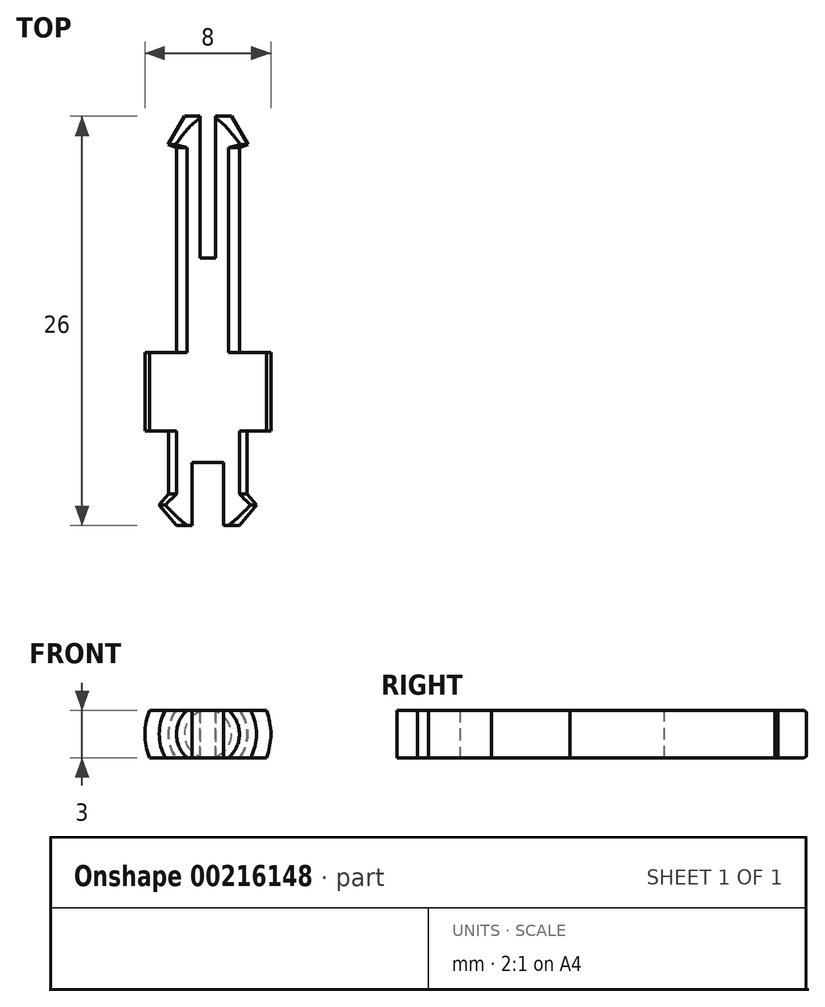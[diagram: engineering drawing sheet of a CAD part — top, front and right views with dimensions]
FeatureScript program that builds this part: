
annotation { "Feature Type Name" : "Feature", "Feature Type Description" : "" }
export const myFeature = defineFeature(function(context is Context, id is Id, definition is map)
    precondition{}
    {
        {
            var Q0;
            Q0=qCreatedBy(makeId("Front.planeOp"),FACE);
            var sketch = newSketch(context, id + "F15", { "sketchPlane" : qUnion([Q0])});
            skCircle(sketch, "E0", {"center": v(0, 0) * mm, "radius": 2.5 * mm});
            skSolve(sketch);
        }
        {
            var Q0;
            Q0=qSketchRegion(id+"F15",true);
            extrude(context, id + "F0", {"entities" : qUnion([Q0]), "depth" : 4 * mm});
        }
        {
            var Q0;
            Q0=qCreatedBy(makeId("Right.planeOp"),FACE);
            var sketch = newSketch(context, id + "F1", { "sketchPlane" : qUnion([Q0])});
            skLineSegment(sketch, "E1", {"start": v(0, 0) * mm, "end": v(-17.97, 0) * mm, "construction": true});
            skLineSegment(sketch, "E2", {"start": v(-4, 0) * mm, "end": v(-4, 2.5) * mm});
            skLineSegment(sketch, "E3", {"start": v(-4, 2.5) * mm, "end": v(-4.7, 3.09) * mm});
            skLineSegment(sketch, "E4", {"start": v(-4.7, 3.09) * mm, "end": v(-6, 2) * mm});
            skLineSegment(sketch, "E5", {"start": v(-6, 2) * mm, "end": v(-6, 0) * mm});
            skLineSegment(sketch, "E6", {"start": v(-6, 0) * mm, "end": v(-4, 0) * mm});
            skSolve(sketch);
        }
        {
            var Q0;
            Q0=qSketchRegion(id+"F1",true);
            var Q1;
            Q1=sQuery(id+"F1.wireOp",EDGE,"E1");
            revolve(context, id + "F2", {"operationType" : NewBodyOperationType.ADD, "entities" : qUnion([Q0]), "axis" : qUnion([Q1]), "revolveType" : RevolveType.FULL});
        }
        {
            var Q0;
            Q0=qCreatedBy(makeId("Top.planeOp"),FACE);
            var sketch = newSketch(context, id + "F3", { "sketchPlane" : qUnion([Q0])});
            skLineSegment(sketch, "E7.bottom", {"start": v(-1, -2) * mm, "end": v(1, -2) * mm});
            skLineSegment(sketch, "E7.top", {"start": v(-1, -9) * mm, "end": v(1, -9) * mm});
            skLineSegment(sketch, "E7.left", {"start": v(-1, -2) * mm, "end": v(-1, -9) * mm});
            skLineSegment(sketch, "E7.right", {"start": v(1, -2) * mm, "end": v(1, -9) * mm});
            skPoint(sketch, "E8", {"position": v(0, -2) * mm});
            skSolve(sketch);
        }
        {
            var Q0;
            Q0=qSketchRegion(id+"F3",true);
            extrude(context, id + "F4", {"entities" : qUnion([Q0]), "operationType" : NewBodyOperationType.REMOVE, "endBound" : BoundingType.SYMMETRIC, "depth" : 7 * mm});
        }
        {
            var Q0;
            Q0=makeQuery(id+"F15.imprint","IMPRINT",FACE,{"disambiguationData":[TD([[makeQuery(id+"F15.imprint","IMPRINT",EDGE,{"derivedFrom":sQuery(id+"F15.wireOp",EDGE,"E0")}),1.0]])]});
            var sketch = newSketch(context, id + "F5", { "sketchPlane" : qUnion([Q0])});
            skCircle(sketch, "E9", {"center": v(0, 0) * mm, "radius": 4 * mm});
            skSolve(sketch);
        }
        {
            var Q0;
            Q0=qSketchRegion(id+"F5",true);
            extrude(context, id + "F6", {"entities" : qUnion([Q0]), "operationType" : NewBodyOperationType.ADD, "oppositeDirection" : true, "depth" : 5 * mm});
        }
        {
            var Q0;
            Q0=makeQuery(id+"F6.opExtrude","CAP_FACE",FACE,{"disambiguationData":[OSD([sQuery(id+"F5.wireOp",EDGE,"E9")])],"isStart":false});
            var sketch = newSketch(context, id + "F7", { "sketchPlane" : qUnion([Q0])});
            skCircle(sketch, "E10", {"center": v(0, 0) * mm, "radius": 2 * mm});
            skSolve(sketch);
        }
        {
            var Q0;
            Q0=qSketchRegion(id+"F7",true);
            extrude(context, id + "F8", {"entities" : qUnion([Q0]), "operationType" : NewBodyOperationType.ADD, "depth" : 13 * mm});
        }
        {
            var Q0;
            Q0=qCreatedBy(makeId("Right.planeOp"),FACE);
            var sketch = newSketch(context, id + "F9", { "sketchPlane" : qUnion([Q0])});
            skLineSegment(sketch, "E11", {"start": v(18, 0) * mm, "end": v(20, 0) * mm});
            skLineSegment(sketch, "E12", {"start": v(20, 0) * mm, "end": v(20, 1.5) * mm});
            skLineSegment(sketch, "E13", {"start": v(20, 1.5) * mm, "end": v(18.2, 2.54) * mm});
            skLineSegment(sketch, "E14", {"start": v(18.2, 2.54) * mm, "end": v(18, 2) * mm});
            skLineSegment(sketch, "E15", {"start": v(18, 2) * mm, "end": v(18, 0) * mm});
            skSolve(sketch);
        }
        {
            var Q0;
            Q0=qSketchRegion(id+"F9",true);
            var Q1;
            Q1=sQuery(id+"F9.wireOp",EDGE,"E11");
            revolve(context, id + "F10", {"operationType" : NewBodyOperationType.ADD, "entities" : qUnion([Q0]), "axis" : qUnion([Q1]), "revolveType" : RevolveType.FULL});
        }
        {
            var Q0;
            Q0=qCreatedBy(makeId("Top.planeOp"),FACE);
            var sketch = newSketch(context, id + "F11", { "sketchPlane" : qUnion([Q0])});
            skLineSegment(sketch, "E16.bottom", {"start": v(-0.5, 22) * mm, "end": v(0.5, 22) * mm});
            skLineSegment(sketch, "E16.top", {"start": v(-0.5, 11) * mm, "end": v(0.5, 11) * mm});
            skLineSegment(sketch, "E16.left", {"start": v(-0.5, 22) * mm, "end": v(-0.5, 11) * mm});
            skLineSegment(sketch, "E16.right", {"start": v(0.5, 22) * mm, "end": v(0.5, 11) * mm});
            skPoint(sketch, "E17", {"position": v(0, 11) * mm});
            skSolve(sketch);
        }
        {
            var Q0;
            Q0=qSketchRegion(id+"F11",true);
            extrude(context, id + "F12", {"entities" : qUnion([Q0]), "operationType" : NewBodyOperationType.REMOVE, "endBound" : BoundingType.SYMMETRIC, "oppositeDirection" : true, "depth" : 25 * mm});
        }
        {
            var Q0;
            Q0=qCreatedBy(makeId("Front.planeOp"),FACE);
            var sketch = newSketch(context, id + "F13", { "sketchPlane" : qUnion([Q0])});
            skLineSegment(sketch, "E18.bottom", {"start": v(-5.5, 6.5) * mm, "end": v(5.5, 6.5) * mm});
            skLineSegment(sketch, "E18.top", {"start": v(-5.5, 1.5) * mm, "end": v(5.5, 1.5) * mm});
            skLineSegment(sketch, "E18.left", {"start": v(-5.5, 6.5) * mm, "end": v(-5.5, 1.5) * mm});
            skLineSegment(sketch, "E18.right", {"start": v(5.5, 6.5) * mm, "end": v(5.5, 1.5) * mm});
            skPoint(sketch, "E19", {"position": v(0, 1.5) * mm});
            skLineSegment(sketch, "E20", {"start": v(-5.87, 0) * mm, "end": v(6.42, 0) * mm, "construction": true});
            skPoint(sketch, "E21.MirrorP", {"position": v(0, -1.5) * mm});
            skLineSegment(sketch, "E22.MirrorCS", {"start": v(-5.5, -6.5) * mm, "end": v(5.5, -6.5) * mm});
            skLineSegment(sketch, "E23.MirrorCS", {"start": v(-5.5, -1.5) * mm, "end": v(5.5, -1.5) * mm});
            skLineSegment(sketch, "E24.MirrorCS", {"start": v(-5.5, -6.5) * mm, "end": v(-5.5, -1.5) * mm});
            skLineSegment(sketch, "E25.MirrorCS", {"start": v(5.5, -6.5) * mm, "end": v(5.5, -1.5) * mm});
            skSolve(sketch);
        }
        {
            var Q0;
            Q0=qSketchRegion(id+"F13",true);
            extrude(context, id + "F14", {"entities" : qUnion([Q0]), "operationType" : NewBodyOperationType.REMOVE, "endBound" : BoundingType.SYMMETRIC, "oppositeDirection" : true, "depth" : 50 * mm});
        }
    });
